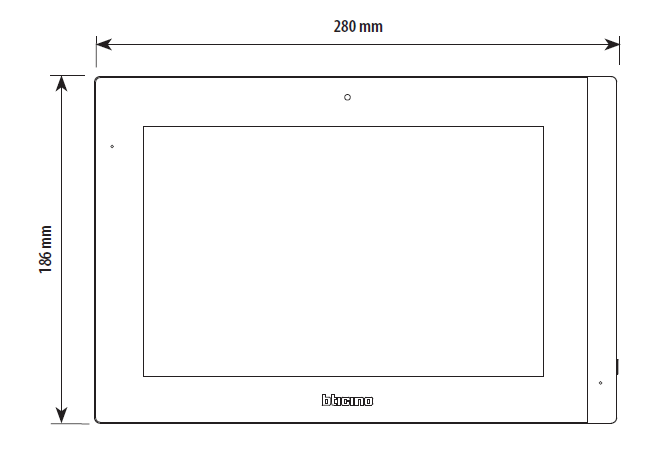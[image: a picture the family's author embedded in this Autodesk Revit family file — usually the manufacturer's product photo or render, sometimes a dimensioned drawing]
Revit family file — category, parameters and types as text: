
# Revit family: Legrand-Hotel_UX_ONE-Thermostat
name_source: partatom
category: Equipement électrique
units: mm (PartAtom-declared; Revit-internal decimal feet)

## family parameters
Configuration du panneau = Deux colonnes, circuits au sein
Cote de connecteur circulaire = Utiliser le diamètre
Couper avec des vides une fois chargée = Non
Hôte = Face
Partagée = Non
Point de calcul de pièce = Non
Type d'élément = Tableau de raccordement

## types (8) — shared parameters
Avec affichage = Oui
Conditions Générale d'Utilisation = https://export.legrand.com
Ecran Tactile = Oui
Elévation par défaut = 1500 mm  [stored 4.92126 ft]
Fabricant = LEGRAND
Fonction ne pas Déranger = Non
Fonctionnement en parallèle possible = Oui
Hauteur = 93 mm  [stored 0.305118 ft]
IK = 04
IP = 20
Largeur = 129 mm  [stored 0.423228 ft]
Matière = Plastique
Réglage manuel de la valeur de consigne = Oui
Site web configurateur = https://uxforhotels.legrand.com
Système de bus radio = Oui
profondeur d'encastrement = 50 mm  [stored 0.164042 ft]

## per-type parameters (varying)
| type | Couleur | Désignation produit | Hauteur pictogrammes | Hauteur vide | Matériau plaque | Matériau écran | Mode de pose | Plaque apparente | Plaque encastrée | Profondeur | Référence / Modèle | Tension |
| Noir 230V Encastré | Noir | HOTEL THERMOSTAT ENCASTRE NOIR 230V | 0 mm  [stored 0 ft] | -40 mm  [stored -0.131234 ft] | LEGRAND_BLACK_PLASTIC | LEGRAND_BLACK_SCREEN | Encastré | Non | Oui | 52 mm | LG-048900 | 230 V AC |
| Noir 230V Apparent | Noir | HOTEL THERMOSTAT SAILLIE NOIR 230V | 16 mm | 0 mm  [stored 0 ft] | LEGRAND_BLACK_PLASTIC | LEGRAND_BLACK_SCREEN | saillie | Oui | Non | 28 mm  [stored 0.0918635 ft] | LG-048901 | 230 V AC |
| Blanc 230V Encastré | Blanc | HOTEL THERMOSTAT ENCASTRE BLANC 230V | 0 mm  [stored 0 ft] | -40 mm  [stored -0.131234 ft] | LEGRAND_WHITE_PLASTIC | LEGRAND_WHITE_SCREEN | Encastré | Non | Oui | 52 mm | LG-048902 | 230 V AC |
| Blanc 230V Apparent | Blanc | HOTEL THERMOSTAT  SAILLIE BLANC 230V | 16 mm | 0 mm  [stored 0 ft] | LEGRAND_WHITE_PLASTIC | LEGRAND_WHITE_SCREEN | saillie | Oui | Non | 28 mm  [stored 0.0918635 ft] | LG-048903 | 230 V AC |
| Noir 24V Encastré | Noir | HOTEL THERMOSTAT  ENCASTRE NOIR 24V | 0 mm  [stored 0 ft] | -40 mm  [stored -0.131234 ft] | LEGRAND_BLACK_PLASTIC | LEGRAND_BLACK_SCREEN | Encastré | Non | Oui | 52 mm | LG-048904 | 24 V |
| Noir 24V Apparent | Noir | HOTEL THERMOSTAT  SAILLIE NOIR 24V | 16 mm | 0 mm  [stored 0 ft] | LEGRAND_BLACK_PLASTIC | LEGRAND_BLACK_SCREEN | saillie | Oui | Non | 28 mm  [stored 0.0918635 ft] | LG-048905 | 24 V |
| Blanc 24V Encastré | Blanc | HOTEL THERMOSTAT  ENCASTRE BLANC 24V | 0 mm  [stored 0 ft] | -40 mm  [stored -0.131234 ft] | LEGRAND_WHITE_PLASTIC | LEGRAND_WHITE_SCREEN | Encastré | Non | Oui | 52 mm | LG-048906 | 24 V |
| Blanc 24V Apparent | Blanc | HOTEL THERMOSTAT  SAILLIE BLANC 24V | 16 mm | 0 mm  [stored 0 ft] | LEGRAND_WHITE_PLASTIC | LEGRAND_WHITE_SCREEN | saillie | Oui | Non | 28 mm  [stored 0.0918635 ft] | LG-048907 | 24 V |

note: [stored X ft] marks values corroborated as IEEE doubles in the binary element streams (Revit-internal decimal feet)
